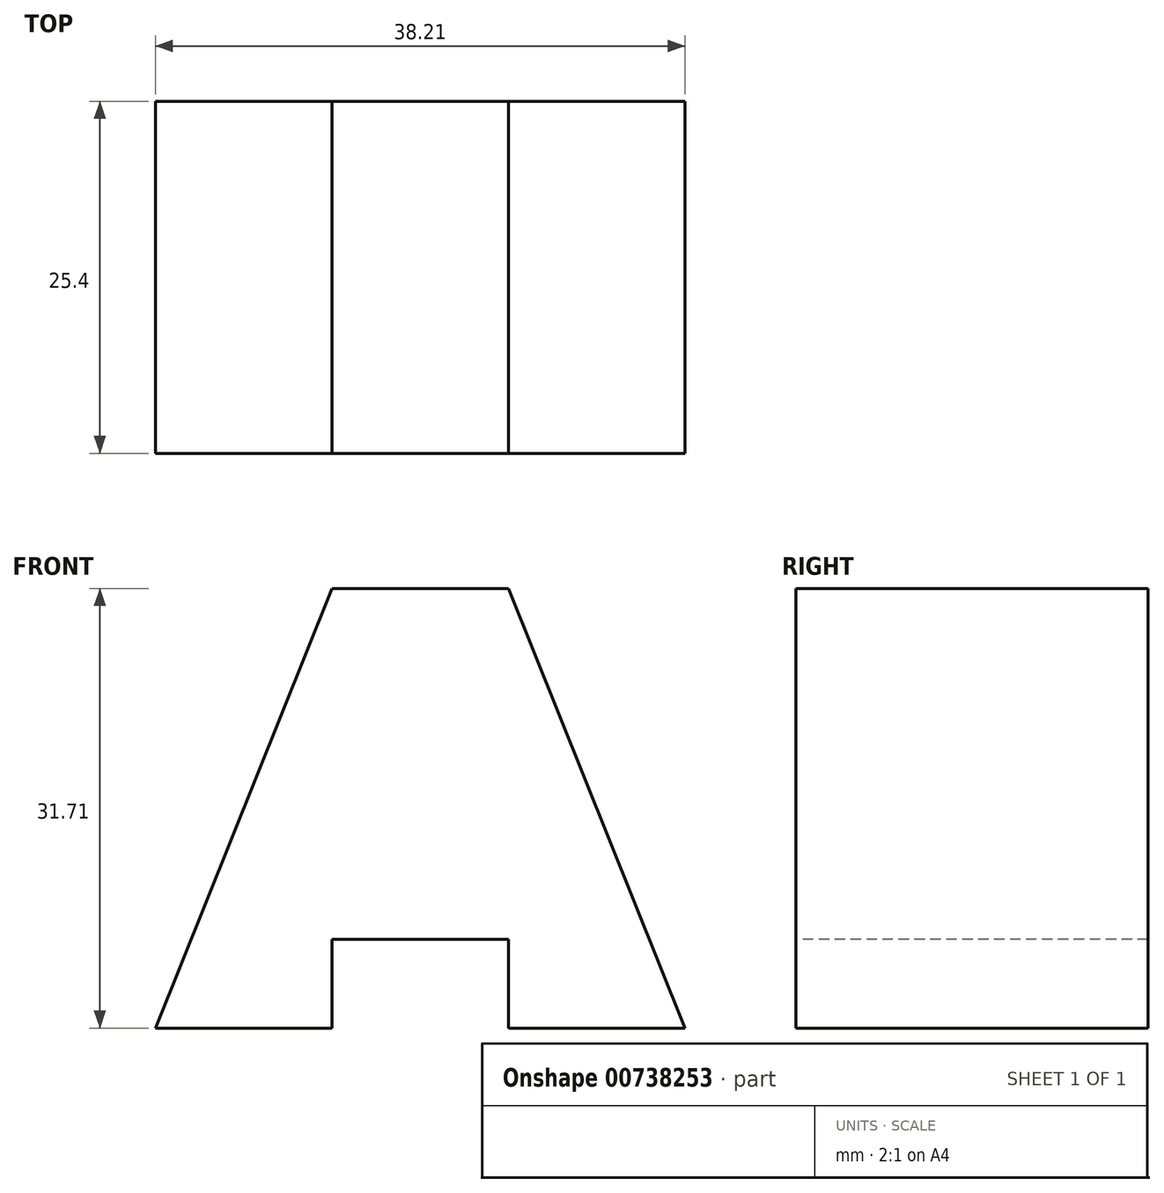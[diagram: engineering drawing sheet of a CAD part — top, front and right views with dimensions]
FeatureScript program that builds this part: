
annotation { "Feature Type Name" : "Feature", "Feature Type Description" : "" }
export const myFeature = defineFeature(function(context is Context, id is Id, definition is map)
    precondition{}
    {
        {
            var Q0;
            Q0=qCreatedBy(makeId("Front.planeOp"),FACE);
            var sketch = newSketch(context, id + "F0", { "sketchPlane" : qUnion([Q0])});
            skLineSegment(sketch, "E0", {"start": v(0, 0) * mm, "end": v(38.2, 0) * mm});
            skLineSegment(sketch, "E1", {"start": v(38.2, 0) * mm, "end": v(38.2, 31.71) * mm});
            skLineSegment(sketch, "E2", {"start": v(0, 0) * mm, "end": v(0, 31.71) * mm});
            skLineSegment(sketch, "E3", {"start": v(0, 31.71) * mm, "end": v(38.2, 31.71) * mm});
            skSolve(sketch);
        }
        {
            var Q0;
            Q0 = qSketchRegion(id + "F0", true);
            extrude(context, id + "F1", {"entities" : qUnion([Q0]), "depth" : 25.4 * mm, "offsetDistance" : 25.4 * mm});
        }
        {
            var Q0;
            Q0=makeQuery(id+"F1.opExtrude","CAP_FACE",FACE,{"disambiguationData":[OSD([sQuery(id+"F0.wireOp",EDGE,"E0"),sQuery(id+"F0.wireOp",EDGE,"E1"),sQuery(id+"F0.wireOp",EDGE,"E2"),sQuery(id+"F0.wireOp",EDGE,"E3")])],"isStart":false});
            var sketch = newSketch(context, id + "F2", { "sketchPlane" : qUnion([Q0])});
            skLineSegment(sketch, "E4", {"start": v(12.74, 31.71) * mm, "end": v(25.56, 31.71) * mm});
            skLineSegment(sketch, "E5", {"start": v(12.74, 31.71) * mm, "end": v(0, 0) * mm});
            skSolve(sketch);
        }
        {
            var Q0;
            {var subQ0=sQuery(id+"F2.wireOp",EDGE,"E5");Q0=makeQuery(id+"F2.imprint","IMPRINT",FACE,{"disambiguationData":[TD([[makeQuery(id+"F2.imprint","IMPRINT",EDGE,{"derivedFrom":subQ0}),-1.0]])]});}
            extrude(context, id + "F3", {"entities" : qUnion([Q0]), "operationType" : NewBodyOperationType.REMOVE, "endBound" : BoundingType.THROUGH_ALL, "oppositeDirection" : true, "depth" : 25.4 * mm, "offsetDistance" : 25.4 * mm});
        }
        {
            var Q0;
            Q0=makeQuery(id+"F1.opExtrude","CAP_FACE",FACE,{"disambiguationData":[OSD([sQuery(id+"F0.wireOp",EDGE,"E0"),sQuery(id+"F0.wireOp",EDGE,"E1"),sQuery(id+"F0.wireOp",EDGE,"E2"),sQuery(id+"F0.wireOp",EDGE,"E3")])],"isStart":false});
            var sketch = newSketch(context, id + "F4", { "sketchPlane" : qUnion([Q0])});
            skLineSegment(sketch, "E6", {"start": v(25.47, 31.71) * mm, "end": v(38.2, 0) * mm});
            skSolve(sketch);
        }
        {
            var Q0;
            {var subQ0=sQuery(id+"F4.wireOp",EDGE,"E6");Q0=makeQuery(id+"F4.imprint","IMPRINT",FACE,{"disambiguationData":[TD([[makeQuery(id+"F4.imprint","IMPRINT",EDGE,{"derivedFrom":subQ0}),1.0]])]});}
            extrude(context, id + "F5", {"entities" : qUnion([Q0]), "operationType" : NewBodyOperationType.REMOVE, "endBound" : BoundingType.THROUGH_ALL, "oppositeDirection" : true, "depth" : 25.4 * mm, "offsetDistance" : 25.4 * mm});
        }
        {
            var Q0;
            Q0=makeQuery(id+"F1.opExtrude","CAP_FACE",FACE,{"disambiguationData":[OSD([sQuery(id+"F0.wireOp",EDGE,"E0"),sQuery(id+"F0.wireOp",EDGE,"E1"),sQuery(id+"F0.wireOp",EDGE,"E2"),sQuery(id+"F0.wireOp",EDGE,"E3")])],"isStart":false});
            var sketch = newSketch(context, id + "F6", { "sketchPlane" : qUnion([Q0])});
            skLineSegment(sketch, "E7", {"start": v(25.47, 0) * mm, "end": v(25.47, 6.41) * mm});
            skLineSegment(sketch, "E8", {"start": v(25.47, 6.41) * mm, "end": v(12.74, 6.41) * mm});
            skLineSegment(sketch, "E9", {"start": v(12.74, 6.41) * mm, "end": v(12.74, 0) * mm});
            skSolve(sketch);
        }
        {
            var Q0;
            {var subQ0=sQuery(id+"F6.wireOp",EDGE,"E7");Q0=makeQuery(id+"F6.imprint","IMPRINT",FACE,{"disambiguationData":[TD([[makeQuery(id+"F6.imprint","IMPRINT",EDGE,{"derivedFrom":subQ0}),1.0]])]});}
            extrude(context, id + "F7", {"entities" : qUnion([Q0]), "operationType" : NewBodyOperationType.REMOVE, "endBound" : BoundingType.THROUGH_ALL, "oppositeDirection" : true, "depth" : 25.4 * mm, "offsetDistance" : 25.4 * mm});
        }
    });
